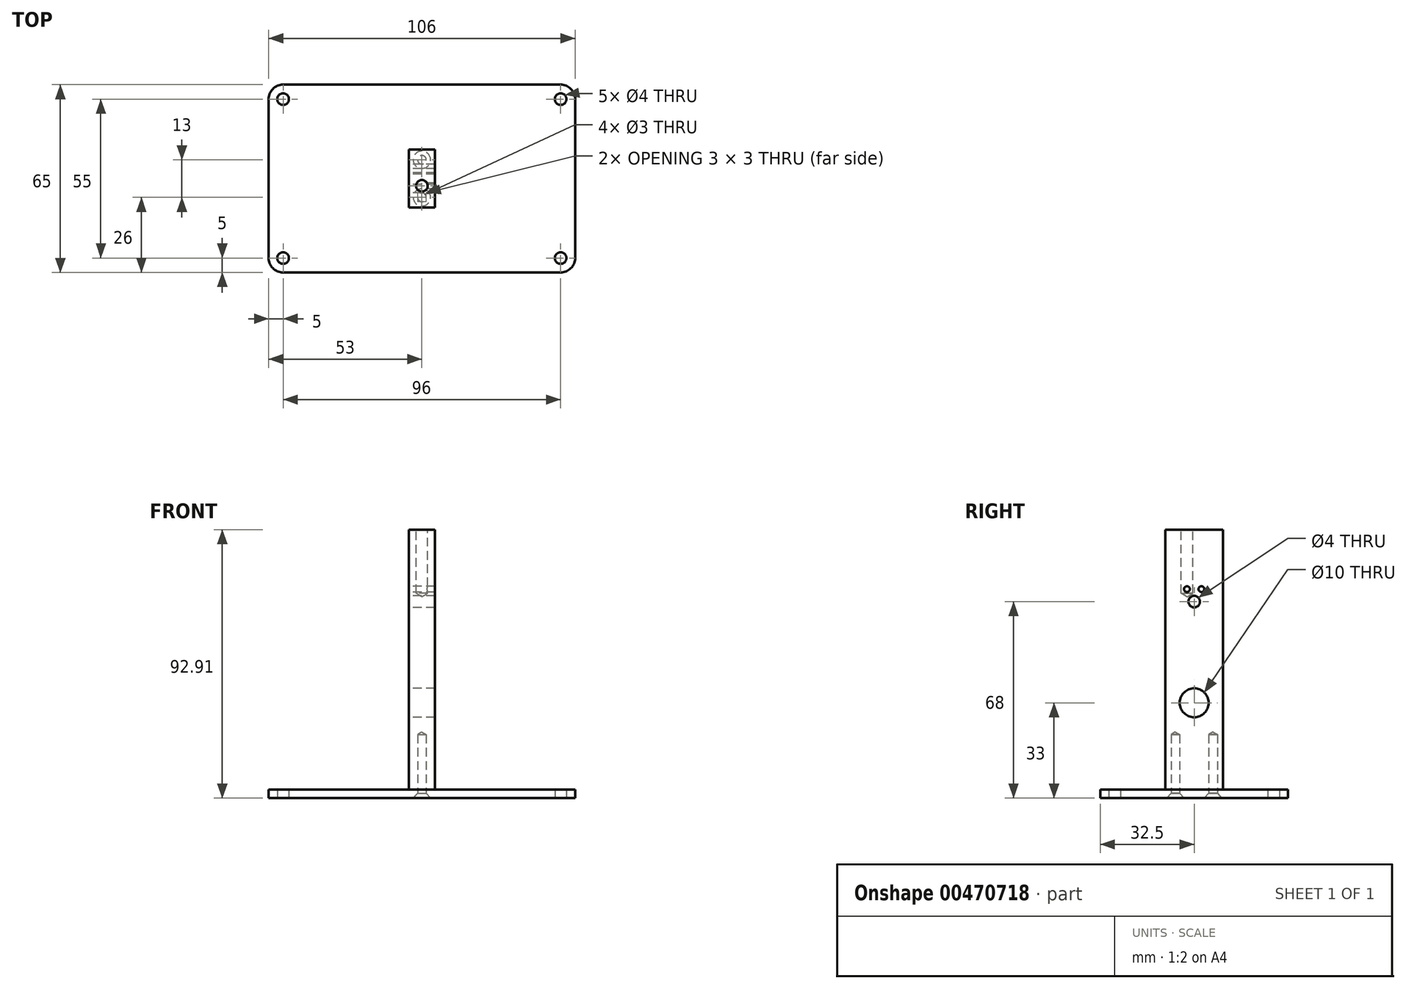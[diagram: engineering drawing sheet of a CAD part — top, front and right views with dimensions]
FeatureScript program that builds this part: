
annotation { "Feature Type Name" : "Feature", "Feature Type Description" : "" }
export const myFeature = defineFeature(function(context is Context, id is Id, definition is map)
    precondition{}
    {
        {
            var Q0;
            Q0=qCreatedBy(makeId("Top.planeOp"),FACE);
            var sketch = newSketch(context, id + "F0", { "sketchPlane" : qUnion([Q0])});
            skLineSegment(sketch, "E0.bottom", {"start": v(48, 32.5) * mm, "end": v(-48, 32.5) * mm});
            skLineSegment(sketch, "E0.top", {"start": v(48, -32.5) * mm, "end": v(-48, -32.5) * mm});
            skLineSegment(sketch, "E0.left", {"start": v(53, 27.5) * mm, "end": v(53, -27.5) * mm});
            skLineSegment(sketch, "E0.right", {"start": v(-53, 27.5) * mm, "end": v(-53, -27.5) * mm});
            skPoint(sketch, "E0.middle", {"position": v(0, 0) * mm});
            skLineSegment(sketch, "E1.bottom", {"start": v(48, 27.5) * mm, "end": v(-48, 27.5) * mm, "construction": true});
            skLineSegment(sketch, "E1.top", {"start": v(48, -27.5) * mm, "end": v(-48, -27.5) * mm, "construction": true});
            skLineSegment(sketch, "E1.left", {"start": v(48, 27.5) * mm, "end": v(48, -27.5) * mm, "construction": true});
            skLineSegment(sketch, "E1.right", {"start": v(-48, 27.5) * mm, "end": v(-48, -27.5) * mm, "construction": true});
            skCircle(sketch, "E2", {"center": v(-48, 27.5) * mm, "radius": 2 * mm});
            skCircle(sketch, "E3", {"center": v(-48, -27.5) * mm, "radius": 2 * mm});
            skCircle(sketch, "E4", {"center": v(48, -27.5) * mm, "radius": 2 * mm});
            skCircle(sketch, "E5", {"center": v(48, 27.5) * mm, "radius": 2 * mm});
            skLineSegment(sketch, "E6", {"start": v(0, 32.5) * mm, "end": v(0, 6.5) * mm, "construction": true});
            skPoint(sketch, "E6.endSnap0", {"position": v(0, 32.5) * mm});
            skPoint(sketch, "E7", {"position": v(0, 6.5) * mm});
            skPoint(sketch, "E8.MirrorP", {"position": v(0, -6.5) * mm});
            skPoint(sketch, "E9.visualSharp", {"position": v(-53, 32.5) * mm});
            skArc(sketch, "E9.filletArc", {"start": v(-48, 32.5) * mm, "mid": v(-51.54, 31.04) * mm, "end": v(-53, 27.5) * mm});
            skPoint(sketch, "E10.visualSharp", {"position": v(-53, -32.5) * mm});
            skArc(sketch, "E10.filletArc", {"start": v(-53, -27.5) * mm, "mid": v(-51.54, -31.04) * mm, "end": v(-48, -32.5) * mm});
            skPoint(sketch, "E11.visualSharp", {"position": v(53, -32.5) * mm});
            skArc(sketch, "E11.filletArc", {"start": v(48, -32.5) * mm, "mid": v(51.54, -31.04) * mm, "end": v(53, -27.5) * mm});
            skPoint(sketch, "E12.visualSharp", {"position": v(53, 32.5) * mm});
            skArc(sketch, "E12.filletArc", {"start": v(53, 27.5) * mm, "mid": v(51.54, 31.04) * mm, "end": v(48, 32.5) * mm});
            skSolve(sketch);
        }
        {
            var Q0;
            Q0=makeQuery(id+"F0.imprint","IMPRINT",FACE,{"disambiguationData":[TD([[makeQuery(id+"F0.imprint","IMPRINT",EDGE,{"derivedFrom":sQuery(id+"F0.wireOp",EDGE,"E0.bottom")}),1.0]])]});
            extrude(context, id + "F1", {"entities" : qUnion([Q0]), "depth" : 3 * mm});
        }
        {
            var Q0;
            Q0=sQuery(id+"F0.wireOp",VERTEX,"E7");
            var Q1;
            Q1=sQuery(id+"F0.wireOp",VERTEX,"E8.MirrorP");
            var Q2;
            Q2=makeQuery(id+"F1.opExtrude","SWEPT_BODY",BODY,{"disambiguationData":[OSD([sQuery(id+"F0.wireOp",EDGE,"E0.bottom"),sQuery(id+"F0.wireOp",EDGE,"E0.top"),sQuery(id+"F0.wireOp",EDGE,"E0.left"),sQuery(id+"F0.wireOp",EDGE,"E0.right"),sQuery(id+"F0.wireOp",EDGE,"E2"),sQuery(id+"F0.wireOp",EDGE,"E3"),sQuery(id+"F0.wireOp",EDGE,"E4"),sQuery(id+"F0.wireOp",EDGE,"E5"),sQuery(id+"F0.wireOp",EDGE,"E9.filletArc"),sQuery(id+"F0.wireOp",EDGE,"E10.filletArc"),sQuery(id+"F0.wireOp",EDGE,"E11.filletArc"),sQuery(id+"F0.wireOp",EDGE,"E12.filletArc")])]});
            hole(context, id + "F2", {"style" : HoleStyle.C_SINK, "endStyle" : HoleEndStyle.THROUGH, "oppositeDirection" : true, "holeDiameter" : 3 * mm, "cSinkDiameter" : 6 * mm, "cSinkAngle" : 82 * degree, "isTappedThrough" : true, "tappedDepth" : 12 * mm, "tapClearance" : 3, "startFromSketch" : true, "locations" : qUnion([Q0, Q1]), "scope" : qUnion([Q2])});
        }
        {
            var Q0;
            Q0=qCreatedBy(makeId("Right.planeOp"),FACE);
            var sketch = newSketch(context, id + "F3", { "sketchPlane" : qUnion([Q0])});
            skLineSegment(sketch, "E13.bottom", {"start": v(-10, 92.91) * mm, "end": v(10, 92.91) * mm});
            skLineSegment(sketch, "E13.top", {"start": v(-10, 3) * mm, "end": v(10, 3) * mm});
            skLineSegment(sketch, "E13.left", {"start": v(-10, 92.91) * mm, "end": v(-10, 3) * mm});
            skLineSegment(sketch, "E13.right", {"start": v(10, 92.91) * mm, "end": v(10, 3) * mm});
            skLineSegment(sketch, "E14.0", {"start": v(27.5, 3) * mm, "end": v(-27.5, 3) * mm, "construction": true});
            skLineSegment(sketch, "E15", {"start": v(0, 3) * mm, "end": v(0, 33) * mm, "construction": true});
            skPoint(sketch, "E15.endSnap0", {"position": v(0, 3) * mm});
            skLineSegment(sketch, "E16", {"start": v(0, 3) * mm, "end": v(0, 68) * mm, "construction": true});
            skCircle(sketch, "E17", {"center": v(0, 68) * mm, "radius": 2 * mm});
            skCircle(sketch, "E18", {"center": v(0, 68) * mm, "radius": 5 * mm, "construction": true});
            skLineSegment(sketch, "E19", {"start": v(0, 92.91) * mm, "end": v(-2.5, 92.91) * mm, "construction": true});
            skLineSegment(sketch, "E20", {"start": v(-2.5, 92.91) * mm, "end": v(-2.5, 72.33) * mm, "construction": true});
            skCircle(sketch, "E21", {"center": v(-2.5, 72.33) * mm, "radius": 1 * mm});
            skCircle(sketch, "E22", {"center": v(0, 33) * mm, "radius": 5 * mm});
            skLineSegment(sketch, "E23", {"start": v(0, 92.91) * mm, "end": v(2.5, 92.91) * mm, "construction": true});
            skLineSegment(sketch, "E24", {"start": v(2.5, 92.91) * mm, "end": v(2.5, 72.33) * mm, "construction": true});
            skCircle(sketch, "E25", {"center": v(2.5, 72.33) * mm, "radius": 1 * mm});
            skSolve(sketch);
        }
        {
            var Q0;
            Q0=makeQuery(id+"F3.imprint","IMPRINT",FACE,{"disambiguationData":[TD([[makeQuery(id+"F3.imprint","IMPRINT",EDGE,{"derivedFrom":sQuery(id+"F3.wireOp",EDGE,"E13.bottom")}),-1.0]])]});
            var Q1;
            Q1=makeQuery(id+"F3.imprint","IMPRINT",FACE,{"disambiguationData":[TD([[makeQuery(id+"F3.imprint","IMPRINT",EDGE,{"derivedFrom":sQuery(id+"F3.wireOp",EDGE,"E21")}),1.0]])]});
            extrude(context, id + "F4", {"entities" : qUnion([Q0, Q1]), "endBound" : BoundingType.SYMMETRIC, "depth" : 9 * mm});
        }
        {
            var Q0;
            Q0=sQuery(id+"F3.wireOp",VERTEX,"E21.center");
            var Q1;
            Q1=makeQuery(id+"F4.opExtrude","SWEPT_BODY",BODY,{"disambiguationData":[OSD([sQuery(id+"F3.wireOp",EDGE,"E13.bottom"),sQuery(id+"F3.wireOp",EDGE,"E13.top"),sQuery(id+"F3.wireOp",EDGE,"E13.left"),sQuery(id+"F3.wireOp",EDGE,"E13.right"),sQuery(id+"F3.wireOp",EDGE,"E17"),sQuery(id+"F3.wireOp",EDGE,"E22"),sQuery(id+"F3.wireOp",EDGE,"E25")])]});
            hole(context, id + "F5", {"style" : HoleStyle.SIMPLE, "endStyle" : HoleEndStyle.THROUGH, "oppositeDirection" : true, "holeDiameter" : 2 * mm, "isTappedThrough" : true, "tappedDepth" : 12 * mm, "tapClearance" : 3, "startFromSketch" : true, "locations" : qUnion([Q0]), "scope" : qUnion([Q1])});
        }
        {
            var Q0;
            Q0=makeQuery(id+"F4.opExtrude","SWEPT_FACE",FACE,{"disambiguationData":[OSD([sQuery(id+"F3.wireOp",EDGE,"E13.bottom")])]});
            var sketch = newSketch(context, id + "F6", { "sketchPlane" : qUnion([Q0])});
            skLineSegment(sketch, "E26.0.0", {"start": v(-4.5, 10) * mm, "end": v(-4.5, -10) * mm});
            skLineSegment(sketch, "E26.0.1", {"start": v(-4.5, -10) * mm, "end": v(4.5, -10) * mm});
            skLineSegment(sketch, "E26.0.2", {"start": v(4.5, -10) * mm, "end": v(4.5, 10) * mm});
            skLineSegment(sketch, "E26.0.3", {"start": v(4.5, 10) * mm, "end": v(-4.5, 10) * mm});
            skLineSegment(sketch, "E27", {"start": v(0, -10) * mm, "end": v(0, -2.5) * mm, "construction": true});
            skPoint(sketch, "E27.endSnap0", {"position": v(0, -10) * mm});
            skPoint(sketch, "E28", {"position": v(0, -2.5) * mm});
            skSolve(sketch);
        }
        {
            var Q0;
            Q0=sQuery(id+"F6.wireOp",VERTEX,"E28");
            var Q1;
            Q1=makeQuery(id+"F4.opExtrude","SWEPT_BODY",BODY,{"disambiguationData":[OSD([sQuery(id+"F3.wireOp",EDGE,"E13.bottom"),sQuery(id+"F3.wireOp",EDGE,"E13.top"),sQuery(id+"F3.wireOp",EDGE,"E13.left"),sQuery(id+"F3.wireOp",EDGE,"E13.right"),sQuery(id+"F3.wireOp",EDGE,"E17"),sQuery(id+"F3.wireOp",EDGE,"E22"),sQuery(id+"F3.wireOp",EDGE,"E25")])]});
            hole(context, id + "F7", {"style" : HoleStyle.SIMPLE, "endStyle" : HoleEndStyle.BLIND, "holeDiameter" : 4 * mm, "holeDepth" : 22 * mm, "isTappedThrough" : true, "tappedDepth" : 12 * mm, "tapClearance" : 3, "startFromSketch" : true, "locations" : qUnion([Q0]), "scope" : qUnion([Q1])});
        }
        {
            var Q0;
            Q0=makeQuery(id+"F0.imprint","IMPRINT",FACE,{"disambiguationData":[TD([[makeQuery(id+"F0.imprint","IMPRINT",EDGE,{"derivedFrom":sQuery(id+"F0.wireOp",EDGE,"E0.bottom")}),1.0]])]});
            var sketch = newSketch(context, id + "F8", { "sketchPlane" : qUnion([Q0])});
            skPoint(sketch, "E29.0", {"position": v(0, -6.5) * mm});
            skPoint(sketch, "E29.1", {"position": v(0, 6.5) * mm});
            skSolve(sketch);
        }
        {
            var Q0;
            Q0=sQuery(id+"F8.wireOp",VERTEX,"E29.0");
            var Q1;
            Q1=sQuery(id+"F8.wireOp",VERTEX,"E29.1");
            var Q2;
            Q2=makeQuery(id+"F4.opExtrude","SWEPT_BODY",BODY,{"disambiguationData":[OSD([sQuery(id+"F3.wireOp",EDGE,"E13.bottom"),sQuery(id+"F3.wireOp",EDGE,"E13.top"),sQuery(id+"F3.wireOp",EDGE,"E13.left"),sQuery(id+"F3.wireOp",EDGE,"E13.right"),sQuery(id+"F3.wireOp",EDGE,"E17"),sQuery(id+"F3.wireOp",EDGE,"E22"),sQuery(id+"F3.wireOp",EDGE,"E25")])]});
            hole(context, id + "F9", {"style" : HoleStyle.SIMPLE, "endStyle" : HoleEndStyle.BLIND, "oppositeDirection" : true, "holeDiameter" : 3 * mm, "holeDepth" : 22 * mm, "isTappedThrough" : true, "tappedDepth" : 12 * mm, "tapClearance" : 3, "startFromSketch" : true, "locations" : qUnion([Q0, Q1]), "scope" : qUnion([Q2])});
        }
    });
